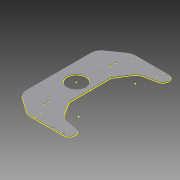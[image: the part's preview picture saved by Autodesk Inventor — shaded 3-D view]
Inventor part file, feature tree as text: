
AUTODESK INVENTOR PART (.ipt)
format: ipt  version: 2013 (Build 170138000, 138)  size: 411,136 bytes
history: native  units: mm
features: extrude x2, sketch x2, other x1
ambient origin geometry x8: Origin, YZ Plane, XZ Plane, XY Plane, X Axis, Y Axis, Z Axis, Center Point
feature tree (5):
  extrude  "Extrusion7"  Depth=50.0mm
  extrude  "Extrusion8"  Depth=100.0mm
  sketch  "Sketch18"  dims[d5=200.0mm d6=100.0mm d7=70.0mm d8=180.0mm d9=20.0mm d10=100.0mm d11=50.0mm d14=50.0mm d15=25.0mm d16=5.0mm d17=5.0mm d18=150.0mm d19=5.0mm d20=5.0mm d21=30.0mm d22=10.0mm d23=6.0mm d24=97.0mm d25=73.0mm d26=4.0mm d27=8.0mm d28=8.0mm d29=7.0mm d30=4.0mm d31=8.0mm d33=8.0mm d34=1.0mm d35=8.0mm d36=4.0mm d37=7.0mm d38=8.0mm d39=4.0mm d40=8.0mm d41=30.0mm d42=8.0mm d43=1.0mm d61=30.0mm d89=8.0mm d90=4.0mm d91=8.0mm d92=4.0mm d93=30.0mm d95=7.0mm d96=5.0mm d97=8.0mm d98=4.0mm d99=8.0mm d100=4.0mm d101=30.0mm d103=7.0mm d104=5.0mm d114=90.0mm d127=97.0mm d128=6.0mm d129=10.0mm d130=73.0mm d131=65.0mm d132=100.0mm d133=200.0mm d134=5.0mm d135=2.5mm d136=50.0mm d137=2.5mm d150=5.0mm d151=5.0mm d152=50.0mm d153=5.0mm d154=5.0mm d155=50.0mm d162=5.0mm d163=5.0mm d164=50.0mm d165=5.0mm d166=5.0mm d167=50.0mm d182=10.0mm d183=6.0mm d184=10.0mm d185=10.0mm d186=10.0mm d187=6.0mm d195=3.0mm d196=0.0mm d197=0.5mm d199=10.0mm d200=10.0mm d201=60.0mm d202=10.0mm d203=0.5mm d204=99.75mm d205=10.0mm d206=10.0mm d207=0.5mm d208=0.5mm d209=60.0mm d210=99.75mm d211=2.0mm d212=0.0mm]
  other  "Profile"
  sketch  "Sketch17"  dims[d1=80.0mm d2=50.0mm]
